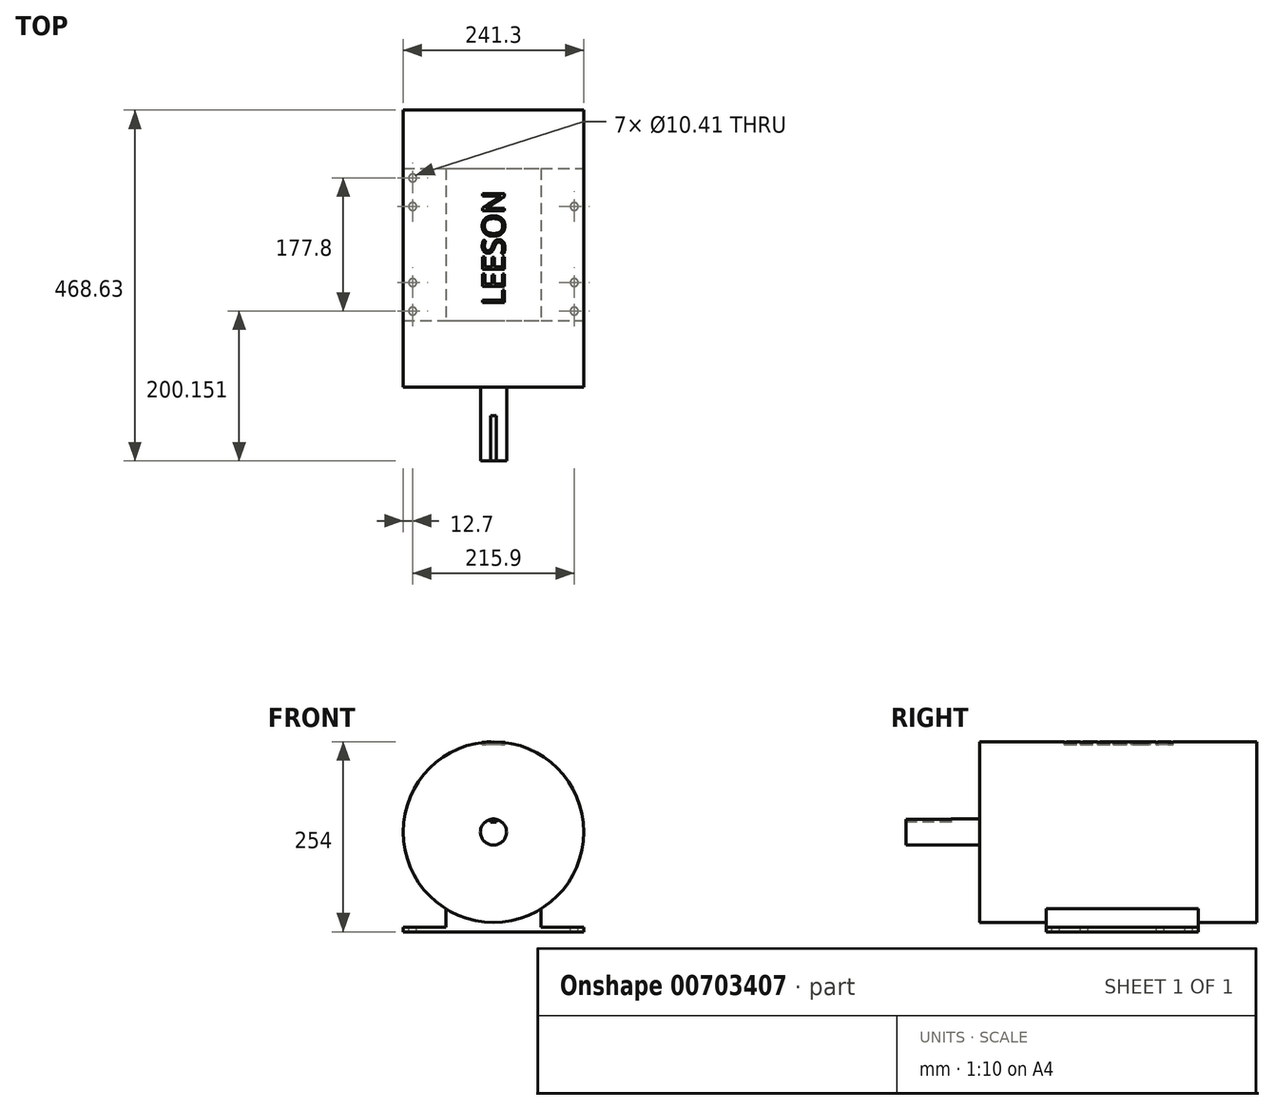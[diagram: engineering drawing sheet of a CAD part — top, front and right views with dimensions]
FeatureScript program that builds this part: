
annotation { "Feature Type Name" : "Feature", "Feature Type Description" : "" }
export const myFeature = defineFeature(function(context is Context, id is Id, definition is map)
    precondition{}
    {
        {
            var Q0;
            Q0=qCreatedBy(makeId("Front.planeOp"),FACE);
            var sketch = newSketch(context, id + "F0", { "sketchPlane" : qUnion([Q0])});
            skCircle(sketch, "E0", {"center": v(0, 0) * mm, "radius": 120.65 * mm});
            skSolve(sketch);
        }
        {
            var Q0;
            Q0=qSketchRegion(id+"F0",true);
            extrude(context, id + "F1", {"entities" : qUnion([Q0]), "endBound" : BoundingType.SYMMETRIC, "depth" : 370.08 * mm, "offsetDistance" : 25.4 * mm});
        }
        {
            var Q0;
            Q0=makeQuery(id+"F1.opExtrude","CAP_FACE",FACE,{"disambiguationData":[OSD([sQuery(id+"F0.wireOp",EDGE,"E0")])],"isStart":false});
            var sketch = newSketch(context, id + "F2", { "sketchPlane" : qUnion([Q0])});
            skCircle(sketch, "E1", {"center": v(0, 0) * mm, "radius": 17.46 * mm});
            skSolve(sketch);
        }
        {
            var Q0;
            Q0=qSketchRegion(id+"F2",true);
            extrude(context, id + "F3", {"entities" : qUnion([Q0]), "operationType" : NewBodyOperationType.ADD, "depth" : 98.55 * mm, "offsetDistance" : 25.4 * mm});
        }
        {
            var Q0;
            Q0=makeQuery(id+"F3.opExtrude","CAP_FACE",FACE,{"disambiguationData":[OSD([sQuery(id+"F2.wireOp",EDGE,"E1")])],"isStart":false});
            var sketch = newSketch(context, id + "F4", { "sketchPlane" : qUnion([Q0])});
            skLineSegment(sketch, "E2.bottom", {"start": v(-3.94, 20.95) * mm, "end": v(3.94, 20.95) * mm});
            skLineSegment(sketch, "E2.top", {"start": v(-3.94, 13.08) * mm, "end": v(3.94, 13.08) * mm});
            skLineSegment(sketch, "E2.left", {"start": v(-3.94, 20.95) * mm, "end": v(-3.94, 13.08) * mm});
            skLineSegment(sketch, "E2.right", {"start": v(3.94, 20.95) * mm, "end": v(3.94, 13.08) * mm});
            skLineSegment(sketch, "E3", {"start": v(0, 13.08) * mm, "end": v(0, 0) * mm, "construction": true});
            skPoint(sketch, "E4", {"position": v(-3.94, 17.01) * mm});
            skSolve(sketch);
        }
        {
            var Q0;
            Q0=qSketchRegion(id+"F4",true);
            extrude(context, id + "F5", {"entities" : qUnion([Q0]), "operationType" : NewBodyOperationType.REMOVE, "oppositeDirection" : true, "depth" : 60.45 * mm, "offsetDistance" : 25.4 * mm});
        }
        {
            var Q0;
            Q0=makeQuery(id+"F1.opExtrude","CAP_FACE",FACE,{"disambiguationData":[OSD([sQuery(id+"F0.wireOp",EDGE,"E0")])],"isStart":false});
            cPlane(context, id + "F6", {"entities" : qUnion([Q0]), "cplaneType" : CPlaneType.OFFSET, "offset" : 88.9 * mm, "oppositeDirection" : true, "width" : 152.4 * mm, "height" : 152.4 * mm});
        }
        {
            var Q0;
            Q0=qCreatedBy(id+"F6.planeOp",FACE);
            var sketch = newSketch(context, id + "F7", { "sketchPlane" : qUnion([Q0])});
            skLineSegment(sketch, "E5.bottom", {"start": v(-120.65, -133.35) * mm, "end": v(120.65, -133.35) * mm});
            skLineSegment(sketch, "E5.top", {"start": v(-120.65, -127) * mm, "end": v(120.65, -127) * mm});
            skLineSegment(sketch, "E5.left", {"start": v(-120.65, -133.35) * mm, "end": v(-120.65, -127) * mm});
            skLineSegment(sketch, "E5.right", {"start": v(120.65, -133.35) * mm, "end": v(120.65, -127) * mm});
            skLineSegment(sketch, "E6", {"start": v(0, -127) * mm, "end": v(0, 0) * mm, "construction": true});
            skLineSegment(sketch, "E7", {"start": v(-63.5, -127) * mm, "end": v(-63.5, -102.59) * mm});
            skLineSegment(sketch, "E8.MirrorCS", {"start": v(63.5, -127) * mm, "end": v(63.5, -102.59) * mm});
            skArc(sketch, "E9", {"start": v(-63.5, -102.59) * mm, "mid": v(0, -120.65) * mm, "end": v(63.5, -102.59) * mm});
            skSolve(sketch);
        }
        {
            var Q0;
            Q0=qSketchRegion(id+"F7",true);
            extrude(context, id + "F8", {"entities" : qUnion([Q0]), "operationType" : NewBodyOperationType.ADD, "oppositeDirection" : true, "depth" : 203.2 * mm, "offsetDistance" : 25.4 * mm});
        }
        {
            var Q0;
            {var subQ0=sQuery(id+"F7.wireOp",EDGE,"E5.top");Q0=makeQuery(id+"F8.opExtrude","SWEPT_FACE",FACE,{"disambiguationData":[OSD([subQ0]),TDD([makeQuery(id+"F7.imprint","IMPRINT",EDGE,{"disambiguationData":[TD([[makeQuery(id+"F7.imprint","INTERSECT",VERTEX,{"derivedFrom":[subQ0,sQuery(id+"F7.wireOp",EDGE,"E5.left")]}),-1.0]])],"derivedFrom":subQ0})])]});}
            var sketch = newSketch(context, id + "F9", { "sketchPlane" : qUnion([Q0])});
            skLineSegment(sketch, "E10.bottom", {"start": v(-107.95, -83.44) * mm, "end": v(107.95, -83.44) * mm, "construction": true});
            skLineSegment(sketch, "E10.top", {"start": v(-107.95, 94.36) * mm, "end": v(107.95, 94.36) * mm, "construction": true});
            skLineSegment(sketch, "E10.left", {"start": v(-107.95, 94.36) * mm, "end": v(-107.95, -83.44) * mm, "construction": true});
            skLineSegment(sketch, "E10.right", {"start": v(107.95, 94.36) * mm, "end": v(107.95, -83.44) * mm, "construction": true});
            skLineSegment(sketch, "E11", {"start": v(0, -83.44) * mm, "end": v(0, 0) * mm, "construction": true});
            skLineSegment(sketch, "E12", {"start": v(-107.95, 56.26) * mm, "end": v(107.95, 56.26) * mm, "construction": true});
            skLineSegment(sketch, "E13", {"start": v(-107.95, -45.34) * mm, "end": v(107.95, -45.34) * mm, "construction": true});
            skLineSegment(sketch, "E14", {"start": v(107.95, -45.34) * mm, "end": v(-107.95, -45.34) * mm, "construction": true});
            skSolve(sketch);
        }
        {
            var Q0;
            Q0=sQuery(id+"F9.wireOp",VERTEX,"E10.top.start");
            var Q1;
            Q1=sQuery(id+"F9.wireOp",VERTEX,"E12.start");
            var Q2;
            Q2=sQuery(id+"F9.wireOp",VERTEX,"E10.bottom.start");
            var Q3;
            Q3=sQuery(id+"F9.wireOp",VERTEX,"E10.bottom.end");
            var Q4;
            Q4=sQuery(id+"F9.wireOp",VERTEX,"E12.end");
            var Q5;
            Q5=sQuery(id+"F9.wireOp",VERTEX,"E10.right.end");
            var Q6;
            Q6=sQuery(id+"F9.wireOp",VERTEX,"E13.start");
            var Q7;
            Q7=sQuery(id+"F9.wireOp",VERTEX,"E13.end");
            var Q8;
            Q8=sQuery(id+"F9.wireOp",VERTEX,"E14.end");
            var Q9;
            Q9=sQuery(id+"F9.wireOp",VERTEX,"E14.start");
            var Q10;
            Q10=makeQuery(id+"F1.opExtrude","SWEPT_BODY",BODY,{"disambiguationData":[OSD([sQuery(id+"F0.wireOp",EDGE,"E0")])]});
            hole(context, id + "F10", {"style" : HoleStyle.SIMPLE, "endStyle" : HoleEndStyle.THROUGH, "holeDiameter" : 10.4 * mm, "majorDiameter" : 6.35 * mm, "isTappedThrough" : true, "tappedDepth" : 12.7 * mm, "tapClearance" : 3, "locations" : qUnion([Q0, Q1, Q2, Q3, Q4, Q5, Q6, Q7, Q8, Q9]), "scope" : qUnion([Q10])});
        }
        {
            var Q0;
            Q0=qCreatedBy(makeId("Top.planeOp"),FACE);
            cPlane(context, id + "F11", {"entities" : qUnion([Q0]), "cplaneType" : CPlaneType.OFFSET, "offset" : 120.65 * mm, "width" : 152.4 * mm, "height" : 152.4 * mm});
        }
        {
            var Q0;
            Q0=qCreatedBy(id+"F11.planeOp",FACE);
            var sketch = newSketch(context, id + "F12", { "sketchPlane" : qUnion([Q0])});
            skText(sketch, "E15", { "text": "LEESON", "fontName": "OpenSans-Regular.ttf"});
            const initialGuessF12  = {"E15": [0.01491, -0.0762, 0, 1, 0.02982]};
            skSetInitialGuess(sketch, initialGuessF12);
            skSolve(sketch);
        }
        {
            var Q0;
            Q0 = qSketchRegion(id + "F12", true);
            var Q1;
            Q1=makeQuery(id+"F1.opExtrude","SWEPT_FACE",FACE,{"disambiguationData":[OSD([sQuery(id+"F0.wireOp",EDGE,"E0")])]});
            extrude(context, id + "F13", {"entities" : qUnion([Q0]), "operationType" : NewBodyOperationType.REMOVE, "endBound" : BoundingType.UP_TO_SURFACE, "oppositeDirection" : true, "depth" : 25.4 * mm, "endBoundEntityFace" : qUnion([Q1]), "hasOffset" : true, "offsetDistance" : 3.17 * mm, "offsetOppositeDirection" : true});
        }
    });
